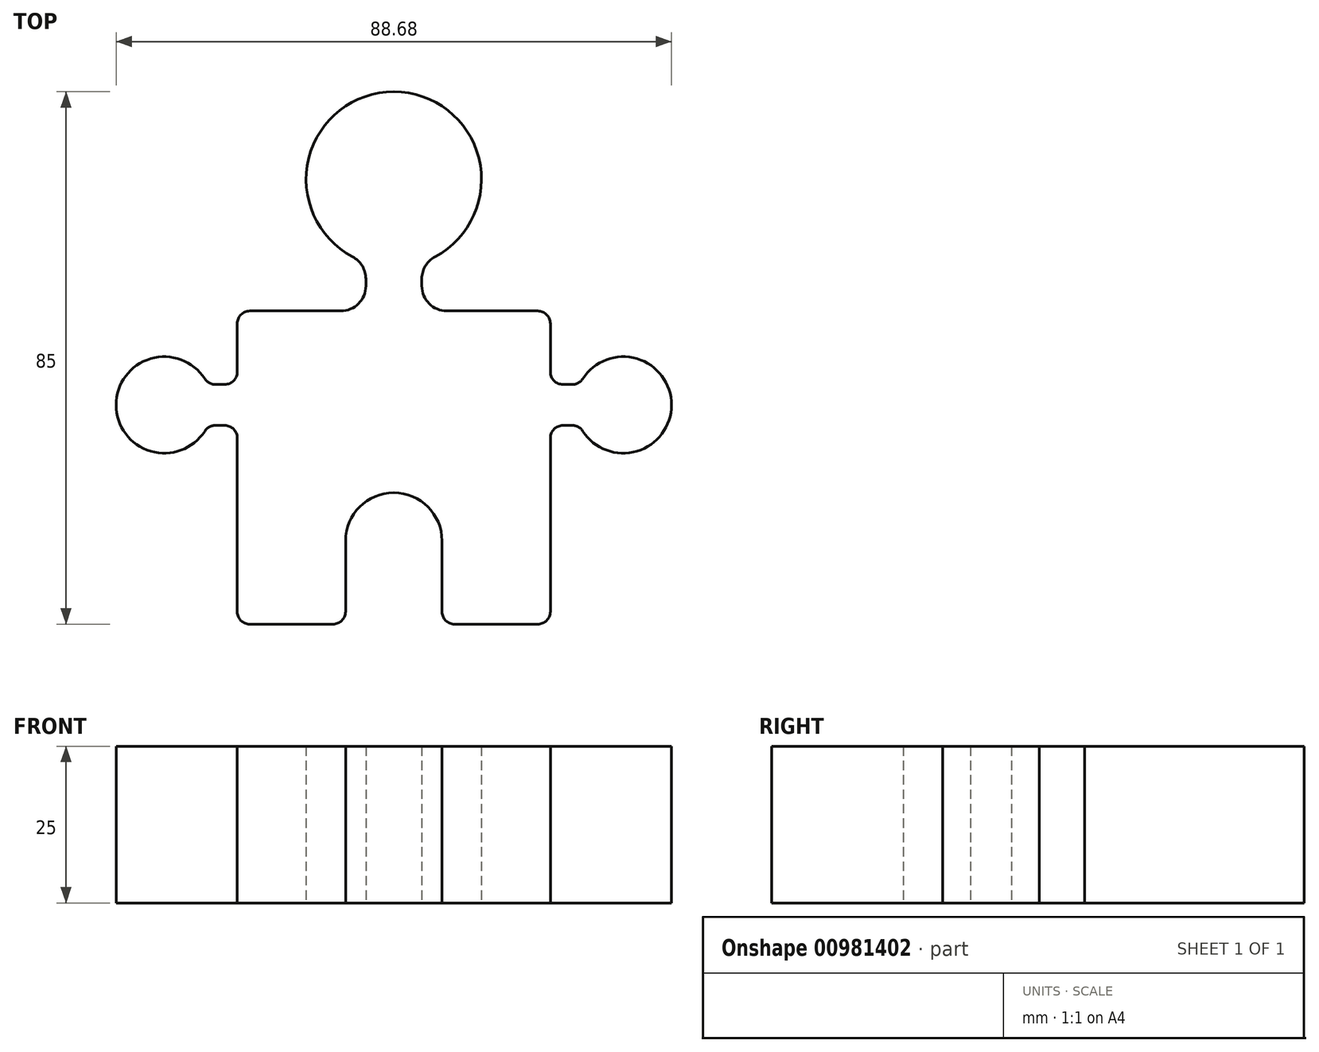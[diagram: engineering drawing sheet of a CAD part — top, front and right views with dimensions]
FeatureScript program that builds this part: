
annotation { "Feature Type Name" : "Feature", "Feature Type Description" : "" }
export const myFeature = defineFeature(function(context is Context, id is Id, definition is map)
    precondition{}
    {
        {
            var Q0;
            Q0=qCreatedBy(makeId("Top.planeOp"),FACE);
            var sketch = newSketch(context, id + "F0", { "sketchPlane" : qUnion([Q0])});
            skLineSegment(sketch, "E0.bottom", {"start": v(-23, -25) * mm, "end": v(-9.7, -25) * mm});
            skLineSegment(sketch, "E0.top", {"start": v(-23, 25) * mm, "end": v(-8.47, 25) * mm});
            skLineSegment(sketch, "E0.left", {"start": v(-25, -23) * mm, "end": v(-25, 4.73) * mm});
            skLineSegment(sketch, "E0.right", {"start": v(25, -23) * mm, "end": v(25, 4.73) * mm});
            skPoint(sketch, "E0.middle", {"position": v(0, 0) * mm});
            skArc(sketch, "E1", {"start": v(-30.18, 14.18) * mm, "mid": v(-44.34, 10) * mm, "end": v(-30.18, 5.82) * mm});
            skLineSegment(sketch, "E2.0", {"start": v(-28.5, 13.27) * mm, "end": v(-27, 13.27) * mm});
            skLineSegment(sketch, "E3.MirrorCS", {"start": v(-28.5, 6.73) * mm, "end": v(-27, 6.73) * mm});
            skLineSegment(sketch, "E4.trimOffspring", {"start": v(-25, 15.27) * mm, "end": v(-25, 23) * mm});
            skPoint(sketch, "E5.visualSharp", {"position": v(-25, 13.27) * mm});
            skArc(sketch, "E5.filletArc", {"start": v(-27, 13.27) * mm, "mid": v(-25.59, 13.86) * mm, "end": v(-25, 15.27) * mm});
            skPoint(sketch, "E6.visualSharp", {"position": v(-25, 6.73) * mm});
            skArc(sketch, "E6.filletArc", {"start": v(-25, 4.73) * mm, "mid": v(-25.59, 6.14) * mm, "end": v(-27, 6.73) * mm});
            skPoint(sketch, "E7.MirrorP", {"position": v(25, 6.5) * mm});
            skLineSegment(sketch, "E8.trimOffspring", {"start": v(25, 15.27) * mm, "end": v(25, 23) * mm});
            skPoint(sketch, "E9.visualSharp", {"position": v(-29.67, 13.27) * mm});
            skArc(sketch, "E9.filletArc", {"start": v(-30.18, 14.18) * mm, "mid": v(-29.46, 13.51) * mm, "end": v(-28.5, 13.27) * mm});
            skPoint(sketch, "E10.visualSharp", {"position": v(-29.67, 6.73) * mm});
            skArc(sketch, "E10.filletArc", {"start": v(-28.5, 6.73) * mm, "mid": v(-29.46, 6.49) * mm, "end": v(-30.18, 5.82) * mm});
            skArc(sketch, "E11", {"start": v(7.7, -11.7) * mm, "mid": v(0, -4) * mm, "end": v(-7.7, -11.7) * mm});
            skLineSegment(sketch, "E12", {"start": v(-7.7, -11.7) * mm, "end": v(-7.7, -23) * mm});
            skLineSegment(sketch, "E13.MirrorCS", {"start": v(7.7, -11.7) * mm, "end": v(7.7, -23) * mm});
            skLineSegment(sketch, "E14.trimOffspring", {"start": v(9.7, -25) * mm, "end": v(23, -25) * mm});
            skArc(sketch, "E15", {"start": v(6.59, 33.65) * mm, "mid": v(0, 60) * mm, "end": v(-6.59, 33.65) * mm});
            skPoint(sketch, "E16.endSnap0", {"position": v(0, 25) * mm});
            skLineSegment(sketch, "E17.0", {"start": v(-4.47, 30.12) * mm, "end": v(-4.47, 29) * mm});
            skLineSegment(sketch, "E18.0", {"start": v(4.47, 30.12) * mm, "end": v(4.47, 29) * mm});
            skPoint(sketch, "E19.orphan", {"position": v(0, 20.24) * mm});
            skLineSegment(sketch, "E20.trimOffspring", {"start": v(8.47, 25) * mm, "end": v(23, 25) * mm});
            skPoint(sketch, "E16.start.orphan", {"position": v(0, 37.16) * mm});
            skPoint(sketch, "E21.visualSharp", {"position": v(-4.47, 25) * mm});
            skArc(sketch, "E21.filletArc", {"start": v(-8.47, 25) * mm, "mid": v(-5.64, 26.17) * mm, "end": v(-4.47, 29) * mm});
            skPoint(sketch, "E22.visualSharp", {"position": v(4.47, 25) * mm});
            skArc(sketch, "E22.filletArc", {"start": v(4.47, 29) * mm, "mid": v(5.64, 26.17) * mm, "end": v(8.47, 25) * mm});
            skPoint(sketch, "E23.visualSharp", {"position": v(4.47, 32.73) * mm});
            skArc(sketch, "E23.filletArc", {"start": v(6.59, 33.65) * mm, "mid": v(5.04, 32.18) * mm, "end": v(4.47, 30.12) * mm});
            skPoint(sketch, "E24.visualSharp", {"position": v(-4.47, 32.73) * mm});
            skArc(sketch, "E24.filletArc", {"start": v(-4.47, 30.12) * mm, "mid": v(-5.04, 32.18) * mm, "end": v(-6.59, 33.65) * mm});
            skPoint(sketch, "E25.visualSharp", {"position": v(-25, 25) * mm});
            skArc(sketch, "E25.filletArc", {"start": v(-23, 25) * mm, "mid": v(-24.41, 24.41) * mm, "end": v(-25, 23) * mm});
            skPoint(sketch, "E26.visualSharp", {"position": v(25, 25) * mm});
            skArc(sketch, "E26.filletArc", {"start": v(25, 23) * mm, "mid": v(24.41, 24.41) * mm, "end": v(23, 25) * mm});
            skPoint(sketch, "E27.visualSharp", {"position": v(25, -25) * mm});
            skArc(sketch, "E27.filletArc", {"start": v(23, -25) * mm, "mid": v(24.41, -24.41) * mm, "end": v(25, -23) * mm});
            skPoint(sketch, "E28.visualSharp", {"position": v(7.7, -25) * mm});
            skArc(sketch, "E28.filletArc", {"start": v(7.7, -23) * mm, "mid": v(8.29, -24.41) * mm, "end": v(9.7, -25) * mm});
            skPoint(sketch, "E29.visualSharp", {"position": v(-7.7, -25) * mm});
            skArc(sketch, "E29.filletArc", {"start": v(-9.7, -25) * mm, "mid": v(-8.29, -24.41) * mm, "end": v(-7.7, -23) * mm});
            skPoint(sketch, "E30.visualSharp", {"position": v(-25, -25) * mm});
            skArc(sketch, "E30.filletArc", {"start": v(-25, -23) * mm, "mid": v(-24.41, -24.41) * mm, "end": v(-23, -25) * mm});
            skLineSegment(sketch, "E31", {"start": v(0, 15.9) * mm, "end": v(0, 5.33) * mm});
            skArc(sketch, "E32.MirrorCS", {"start": v(27, 13.27) * mm, "mid": v(25.59, 13.86) * mm, "end": v(25, 15.27) * mm});
            skLineSegment(sketch, "E33.MirrorCS", {"start": v(28.5, 13.27) * mm, "end": v(27, 13.27) * mm});
            skArc(sketch, "E34.MirrorCS", {"start": v(30.18, 14.18) * mm, "mid": v(29.46, 13.51) * mm, "end": v(28.5, 13.27) * mm});
            skArc(sketch, "E35.MirrorCS", {"start": v(30.18, 14.18) * mm, "mid": v(44.34, 10) * mm, "end": v(30.18, 5.82) * mm});
            skArc(sketch, "E36.MirrorCS", {"start": v(28.5, 6.73) * mm, "mid": v(29.46, 6.49) * mm, "end": v(30.18, 5.82) * mm});
            skLineSegment(sketch, "E37.MirrorCS", {"start": v(28.5, 6.73) * mm, "end": v(27, 6.73) * mm});
            skArc(sketch, "E38.MirrorCS", {"start": v(25, 4.73) * mm, "mid": v(25.59, 6.14) * mm, "end": v(27, 6.73) * mm});
            skSolve(sketch);
        }
        {
            var Q0;
            Q0=makeQuery(id+"F0.imprint","IMPRINT",FACE,{"disambiguationData":[TD([[makeQuery(id+"F0.imprint","IMPRINT",EDGE,{"derivedFrom":sQuery(id+"F0.wireOp",EDGE,"E0.bottom")}),1.0]])]});
            extrude(context, id + "F1", {"entities" : qUnion([Q0]), "depth" : 25 * mm, "offsetDistance" : 25 * mm});
        }
    });
